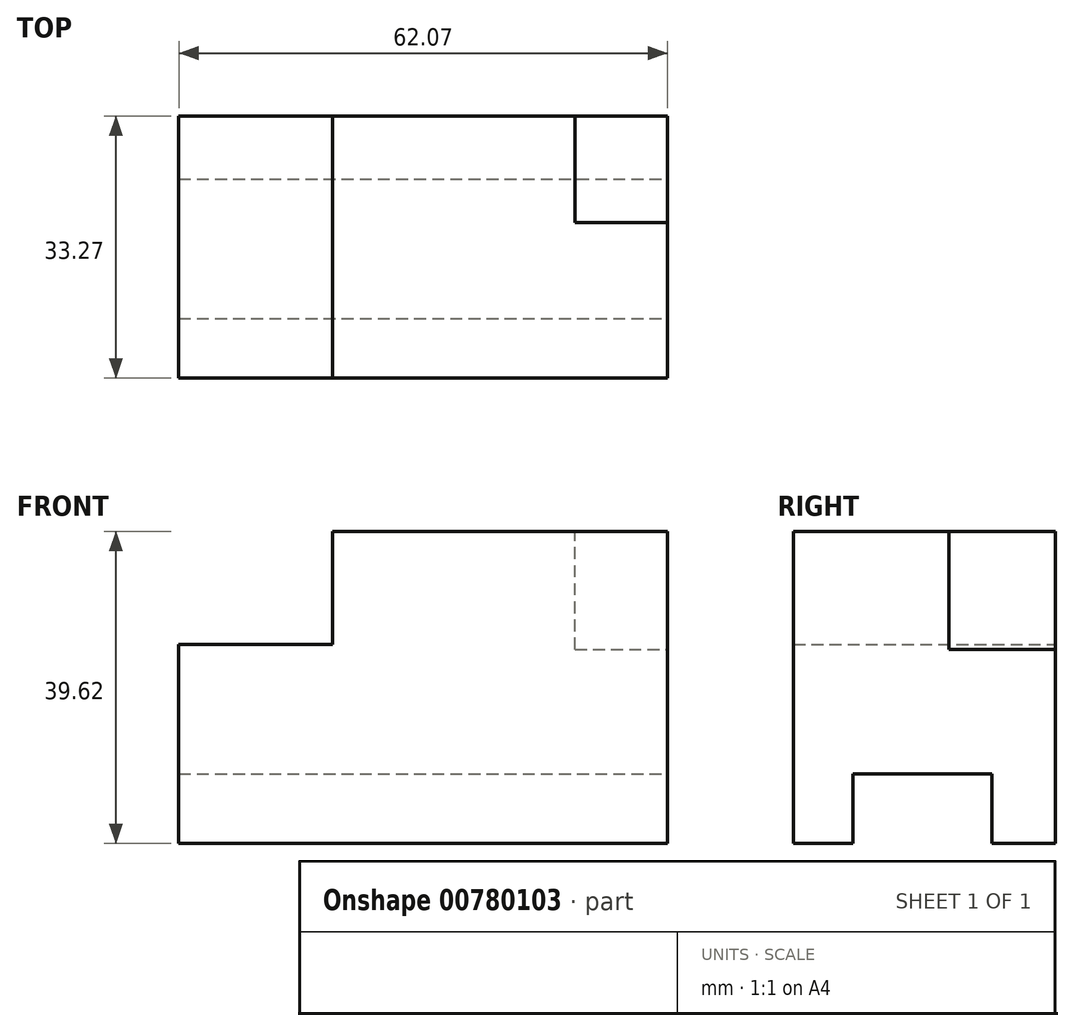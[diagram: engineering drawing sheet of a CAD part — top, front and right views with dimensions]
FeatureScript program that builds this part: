
annotation { "Feature Type Name" : "Feature", "Feature Type Description" : "" }
export const myFeature = defineFeature(function(context is Context, id is Id, definition is map)
    precondition{}
    {
        {
            var Q0;
            Q0=qCreatedBy(makeId("Front.planeOp"),FACE);
            var sketch = newSketch(context, id + "F0", { "sketchPlane" : qUnion([Q0])});
            skLineSegment(sketch, "E0", {"start": v(0, 0) * mm, "end": v(42.52, 0) * mm});
            skLineSegment(sketch, "E1", {"start": v(42.52, 0) * mm, "end": v(42.52, -39.62) * mm});
            skLineSegment(sketch, "E2", {"start": v(42.52, -39.62) * mm, "end": v(-19.55, -39.62) * mm});
            skLineSegment(sketch, "E3", {"start": v(-19.55, -39.62) * mm, "end": v(-19.55, -14.33) * mm});
            skLineSegment(sketch, "E4", {"start": v(-19.55, -14.33) * mm, "end": v(0, -14.33) * mm});
            skLineSegment(sketch, "E5", {"start": v(0, 0) * mm, "end": v(0, -14.33) * mm});
            skSolve(sketch);
        }
        {
            var Q0;
            Q0=makeQuery(id+"F0.imprint","IMPRINT",FACE,{"disambiguationData":[TD([[makeQuery(id+"F0.imprint","IMPRINT",EDGE,{"derivedFrom":sQuery(id+"F0.wireOp",EDGE,"E0")}),-1.0]])]});
            extrude(context, id + "F1", {"entities" : qUnion([Q0]), "depth" : 33.27 * mm, "offsetDistance" : 25.4 * mm});
        }
        {
            var Q0;
            Q0=makeQuery(id+"F1.opExtrude","SWEPT_FACE",FACE,{"disambiguationData":[OSD([sQuery(id+"F0.wireOp",EDGE,"E0")])]});
            var sketch = newSketch(context, id + "F2", { "sketchPlane" : qUnion([Q0])});
            skLineSegment(sketch, "E6.bottom", {"start": v(30.77, -13.54) * mm, "end": v(42.52, -13.54) * mm});
            skLineSegment(sketch, "E6.top", {"start": v(30.77, 0) * mm, "end": v(42.52, 0) * mm});
            skLineSegment(sketch, "E6.left", {"start": v(30.77, -13.54) * mm, "end": v(30.77, 0) * mm});
            skLineSegment(sketch, "E6.right", {"start": v(42.52, -13.54) * mm, "end": v(42.52, 0) * mm});
            skPoint(sketch, "E6.middle", {"position": v(36.65, -6.77) * mm});
            skSolve(sketch);
        }
        {
            var Q0;
            Q0=makeQuery(id+"F2.imprint","IMPRINT",FACE,{"disambiguationData":[TD([[makeQuery(id+"F2.imprint","IMPRINT",EDGE,{"derivedFrom":sQuery(id+"F2.wireOp",EDGE,"E6.bottom")}),1.0]])]});
            extrude(context, id + "F3", {"entities" : qUnion([Q0]), "operationType" : NewBodyOperationType.REMOVE, "oppositeDirection" : true, "depth" : 15 * mm, "offsetDistance" : 25.4 * mm});
        }
        {
            var Q0;
            Q0=makeQuery(id+"F1.opExtrude","SWEPT_FACE",FACE,{"disambiguationData":[OSD([sQuery(id+"F0.wireOp",EDGE,"E1")])]});
            var sketch = newSketch(context, id + "F4", { "sketchPlane" : qUnion([Q0])});
            skLineSegment(sketch, "E7.bottom", {"start": v(-25.7, -30.78) * mm, "end": v(-8.03, -30.78) * mm});
            skLineSegment(sketch, "E7.top", {"start": v(-25.7, -39.62) * mm, "end": v(-8.03, -39.62) * mm});
            skLineSegment(sketch, "E7.left", {"start": v(-25.7, -30.78) * mm, "end": v(-25.7, -39.62) * mm});
            skLineSegment(sketch, "E7.right", {"start": v(-8.03, -30.78) * mm, "end": v(-8.03, -39.62) * mm});
            skSolve(sketch);
        }
        {
            var Q0;
            Q0 = qSketchRegion(id + "F4", true);
            extrude(context, id + "F5", {"entities" : qUnion([Q0]), "operationType" : NewBodyOperationType.REMOVE, "oppositeDirection" : true, "depth" : 84.84 * mm, "offsetDistance" : 25.4 * mm});
        }
    });
